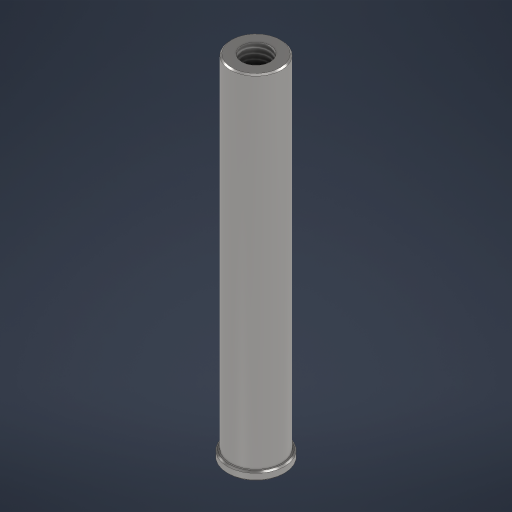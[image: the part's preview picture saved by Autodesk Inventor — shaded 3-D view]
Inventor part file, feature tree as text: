
AUTODESK INVENTOR PART (.ipt)
format: ipt  version: 2024.1 (Build 281209000, 209)  size: 194,048 bytes
history: native  units: mm
features: extrude x3, chamfer x2, thread x1
ambient origin geometry x8: Origin, YZ Plane, XZ Plane, XY Plane, X Axis, Y Axis, Z Axis, Center Point
bodies: Solid1 (feature_tree)
feature tree (6):
  extrude  "Extrusion1"  Depth=5.0mm
  chamfer  "Chamfer1"  Distance=0.75mm
  extrude  "Extrusion2"  Depth=0.125mm TaperAngle=45.0deg
  extrude  "Extrusion3"  Depth=4.5mm
  thread  "Thread1"  [1 undecoded]
  chamfer  "Chamfer2"  Distance=2.5mm
note: 1 required parameter value undecoded (feature->parameter linkage not recoverable at this tier; creation-order binding heuristic only, values carry confidence <= 0.55)
